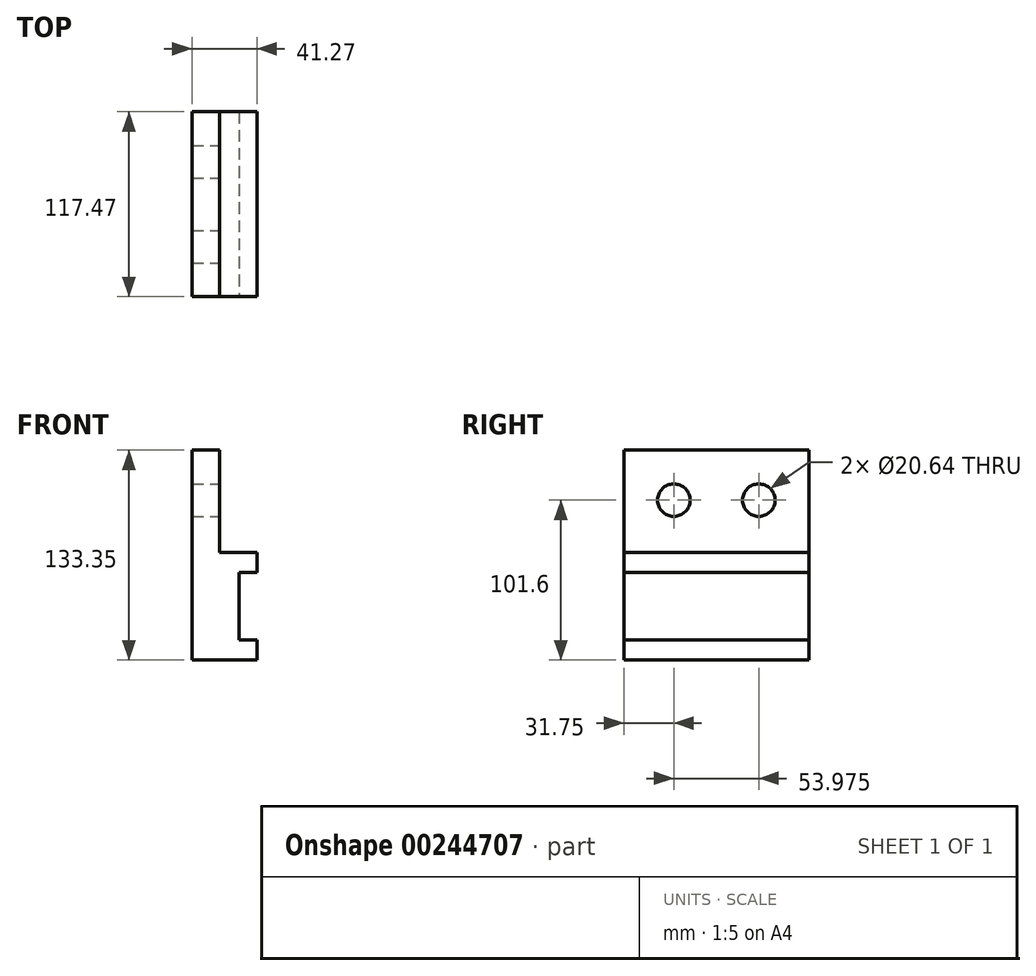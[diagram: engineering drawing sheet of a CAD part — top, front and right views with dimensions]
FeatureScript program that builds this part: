
annotation { "Feature Type Name" : "Feature", "Feature Type Description" : "" }
export const myFeature = defineFeature(function(context is Context, id is Id, definition is map)
    precondition{}
    {
        {
            var Q0;
            Q0=qCreatedBy(makeId("Front.planeOp"),FACE);
            var sketch = newSketch(context, id + "F0", { "sketchPlane" : qUnion([Q0])});
            skLineSegment(sketch, "E0", {"start": v(0, 0) * mm, "end": v(0, 133.35) * mm});
            skLineSegment(sketch, "E1", {"start": v(0, 0) * mm, "end": v(41.28, 0) * mm});
            skLineSegment(sketch, "E2", {"start": v(41.28, 0) * mm, "end": v(41.28, 12.7) * mm});
            skLineSegment(sketch, "E3", {"start": v(41.28, 12.7) * mm, "end": v(30.16, 12.7) * mm});
            skLineSegment(sketch, "E4", {"start": v(30.16, 12.7) * mm, "end": v(30.16, 55.56) * mm});
            skLineSegment(sketch, "E5", {"start": v(30.16, 55.56) * mm, "end": v(41.28, 55.56) * mm});
            skLineSegment(sketch, "E6", {"start": v(41.28, 55.56) * mm, "end": v(41.28, 68.26) * mm});
            skLineSegment(sketch, "E7", {"start": v(0, 133.35) * mm, "end": v(17.46, 133.35) * mm});
            skLineSegment(sketch, "E8", {"start": v(17.46, 133.35) * mm, "end": v(17.46, 68.26) * mm});
            skLineSegment(sketch, "E9", {"start": v(41.28, 68.26) * mm, "end": v(17.46, 68.26) * mm});
            skSolve(sketch);
        }
        {
            var Q0;
            Q0=makeQuery(id+"F0.imprint","IMPRINT",FACE,{"disambiguationData":[TD([[makeQuery(id+"F0.imprint","IMPRINT",EDGE,{"derivedFrom":sQuery(id+"F0.wireOp",EDGE,"E0")}),-1.0]])]});
            extrude(context, id + "F1", {"entities" : qUnion([Q0]), "oppositeDirection" : true, "depth" : 117.47 * mm});
        }
        {
            var Q0;
            Q0=makeQuery(id+"F1.opExtrude","SWEPT_FACE",FACE,{"disambiguationData":[OSD([sQuery(id+"F0.wireOp",EDGE,"E8")])]});
            var sketch = newSketch(context, id + "F2", { "sketchPlane" : qUnion([Q0])});
            skCircle(sketch, "E10", {"center": v(31.75, 101.6) * mm, "radius": 10.32 * mm});
            skCircle(sketch, "E11", {"center": v(85.72, 101.6) * mm, "radius": 10.32 * mm});
            skPoint(sketch, "E12.end.orphan", {"position": v(85.72, 133.35) * mm});
            skPoint(sketch, "E12.start.orphan", {"position": v(31.75, 133.35) * mm});
            skPoint(sketch, "E13.orphan", {"position": v(31.75, 68.26) * mm});
            skSolve(sketch);
        }
        {
            var Q0;
            Q0=makeQuery(id+"F2.imprint","IMPRINT",FACE,{"disambiguationData":[TD([[makeQuery(id+"F2.imprint","IMPRINT",EDGE,{"derivedFrom":sQuery(id+"F2.wireOp",EDGE,"E11")}),1.0]])]});
            var Q1;
            Q1=makeQuery(id+"F2.imprint","IMPRINT",FACE,{"disambiguationData":[TD([[makeQuery(id+"F2.imprint","IMPRINT",EDGE,{"derivedFrom":sQuery(id+"F2.wireOp",EDGE,"E10")}),1.0]])]});
            extrude(context, id + "F3", {"entities" : qUnion([Q0, Q1]), "operationType" : NewBodyOperationType.REMOVE, "oppositeDirection" : true, "depth" : 17.46 * mm});
        }
    });
